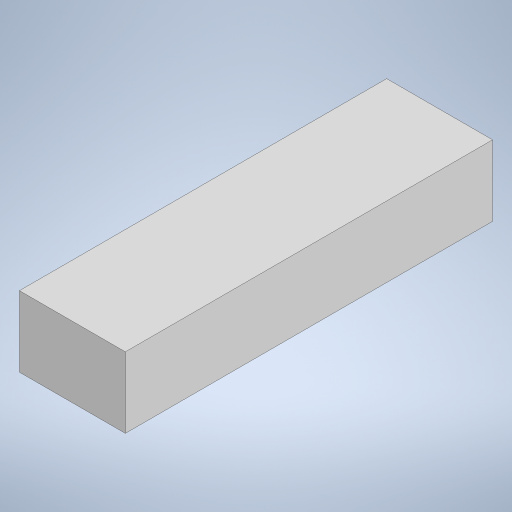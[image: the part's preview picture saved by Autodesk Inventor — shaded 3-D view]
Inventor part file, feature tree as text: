
AUTODESK INVENTOR PART (.ipt)
format: ipt  version: 2024 (Build 280153000, 153)  size: 189,952 bytes
history: native  units: mm
features: extrude x1, sketch x1
ambient origin geometry x8: Origin, YZ Plane, XZ Plane, XY Plane, X Axis, Y Axis, Z Axis, Center Point
bodies: Solid1 (feature_tree)
feature tree (2):
  extrude  "Extrusion1"  Depth=104.0mm
  sketch  "Sketch1"  dims[d0=30.0mm d1=104.0mm d2=20.0mm d3=0.0mm]
